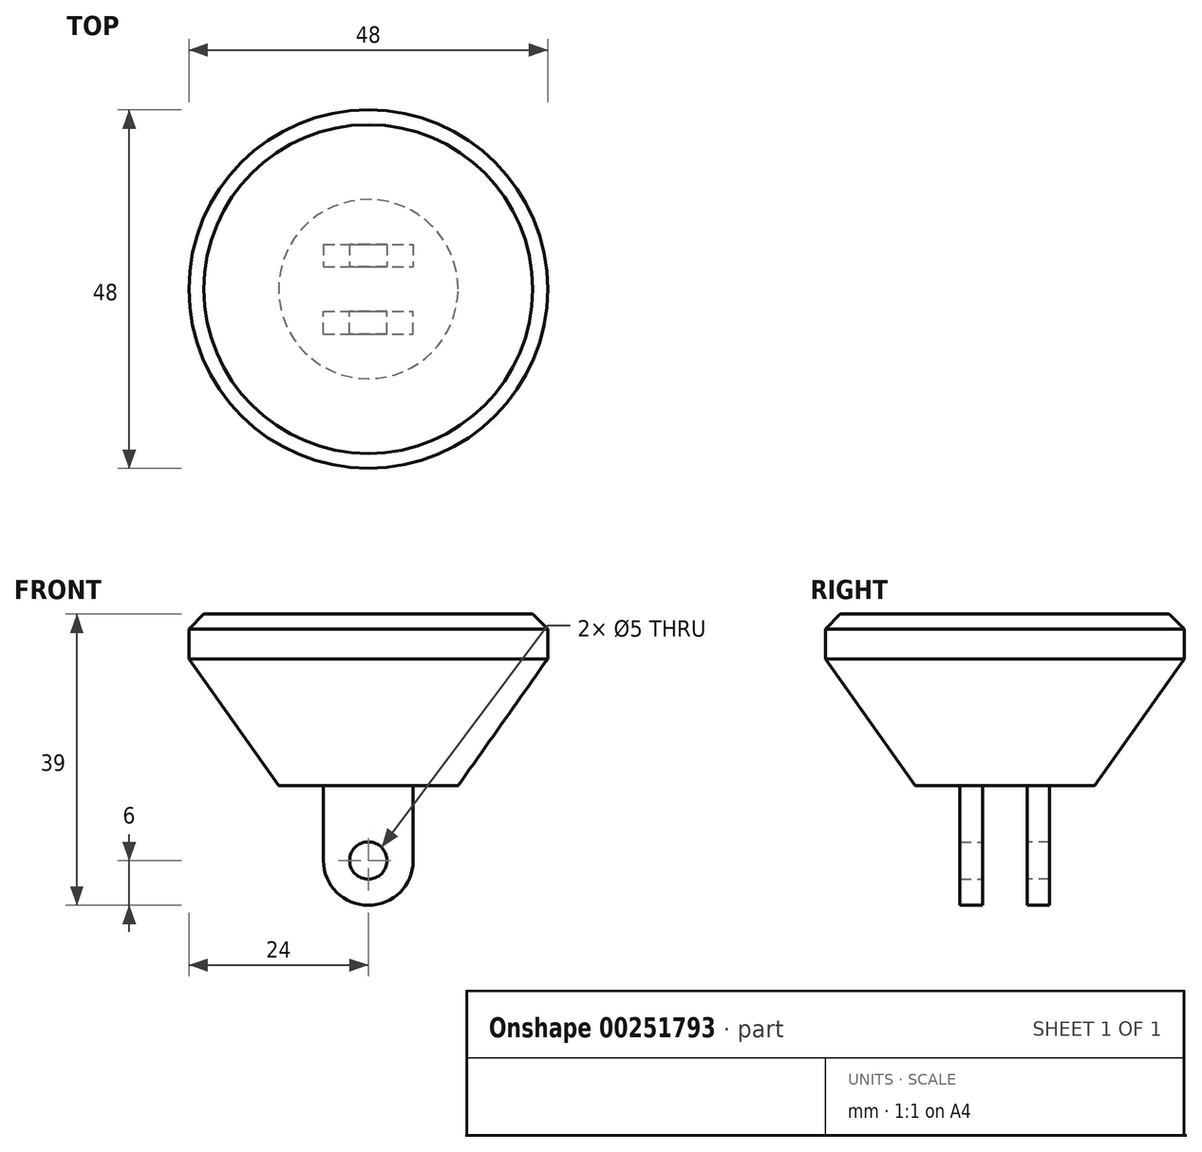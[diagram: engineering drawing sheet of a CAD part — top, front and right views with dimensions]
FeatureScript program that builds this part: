
annotation { "Feature Type Name" : "Feature", "Feature Type Description" : "" }
export const myFeature = defineFeature(function(context is Context, id is Id, definition is map)
    precondition{}
    {
        {
            var Q0;
            Q0=qCreatedBy(makeId("Top.planeOp"),FACE);
            cPlane(context, id + "F0", {"entities" : qUnion([Q0]), "cplaneType" : CPlaneType.OFFSET, "offset" : 2 * mm, "width" : 150 * mm, "height" : 150 * mm});
        }
        {
            var Q0;
            Q0=qCreatedBy(makeId("Top.planeOp"),FACE);
            cPlane(context, id + "F1", {"entities" : qUnion([Q0]), "cplaneType" : CPlaneType.OFFSET, "offset" : 4 * mm, "oppositeDirection" : true, "width" : 150 * mm, "height" : 150 * mm});
        }
        {
            var Q0;
            Q0=qCreatedBy(makeId("Top.planeOp"),FACE);
            cPlane(context, id + "F2", {"entities" : qUnion([Q0]), "cplaneType" : CPlaneType.OFFSET, "offset" : 21 * mm, "oppositeDirection" : true, "width" : 150 * mm, "height" : 150 * mm});
        }
        {
            var Q0;
            Q0=qCreatedBy(id+"F0.planeOp",FACE);
            var sketch = newSketch(context, id + "F3", { "sketchPlane" : qUnion([Q0])});
            skCircle(sketch, "E0", {"center": v(0, 0) * mm, "radius": 22 * mm});
            skSolve(sketch);
        }
        {
            var Q0;
            Q0=qCreatedBy(id+"F1.planeOp",FACE);
            var sketch = newSketch(context, id + "F4", { "sketchPlane" : qUnion([Q0])});
            skCircle(sketch, "E1", {"center": v(0, 0) * mm, "radius": 24 * mm});
            skSolve(sketch);
        }
        {
            var Q0;
            Q0=qCreatedBy(makeId("Top.planeOp"),FACE);
            var sketch = newSketch(context, id + "F5", { "sketchPlane" : qUnion([Q0])});
            skCircle(sketch, "E2", {"center": v(0, 0) * mm, "radius": 24 * mm});
            skSolve(sketch);
        }
        {
            var Q0;
            Q0=qCreatedBy(id+"F2.planeOp",FACE);
            var sketch = newSketch(context, id + "F6", { "sketchPlane" : qUnion([Q0])});
            skCircle(sketch, "E3", {"center": v(0, 0) * mm, "radius": 12 * mm});
            skSolve(sketch);
        }
        {
            var Q0;
            Q0 = qSketchRegion(id + "F6", true);
            var Q1;
            Q1 = qSketchRegion(id + "F4", true);
            loft(context, id + "F7", {"sheetProfilesArray" : [{ "sheetProfileEntities" : qUnion([Q0]) }, { "sheetProfileEntities" : qUnion([Q1]) }]});
        }
        {
            var Q1;
            Q1=makeQuery(id+"F7.opLoft","CAP_FACE",FACE,{"disambiguationData":[OSD([makeQuery(id+"F4.imprint","IMPRINT",FACE,{"disambiguationData":[TD([[makeQuery(id+"F4.imprint","IMPRINT",EDGE,{"derivedFrom":sQuery(id+"F4.wireOp",EDGE,"E1")}),1.0]])]})])],"isStart":true});
            var Q2;
            Q2=makeQuery(id+"F5.imprint","IMPRINT",FACE,{"disambiguationData":[TD([[makeQuery(id+"F5.imprint","IMPRINT",EDGE,{"derivedFrom":sQuery(id+"F5.wireOp",EDGE,"E2")}),1.0]])]});
            loft(context, id + "F8", {"operationType" : NewBodyOperationType.ADD, "sheetProfilesArray" : [{ "sheetProfileEntities" : qUnion([Q1]) }, { "sheetProfileEntities" : qUnion([Q2]) }]});
        }
        {
            var Q1;
            Q1=makeQuery(id+"F8.opLoft","CAP_FACE",FACE,{"disambiguationData":[OSD([makeQuery(id+"F5.imprint","IMPRINT",FACE,{"disambiguationData":[TD([[makeQuery(id+"F5.imprint","IMPRINT",EDGE,{"derivedFrom":sQuery(id+"F5.wireOp",EDGE,"E2")}),1.0]])]})])],"isStart":true});
            var Q2;
            Q2=makeQuery(id+"F3.imprint","IMPRINT",FACE,{"disambiguationData":[TD([[makeQuery(id+"F3.imprint","IMPRINT",EDGE,{"derivedFrom":sQuery(id+"F3.wireOp",EDGE,"E0")}),1.0]])]});
            loft(context, id + "F9", {"operationType" : NewBodyOperationType.ADD, "sheetProfilesArray" : [{ "sheetProfileEntities" : qUnion([Q1]) }, { "sheetProfileEntities" : qUnion([Q2]) }]});
        }
        {
            var Q0;
            Q0=makeQuery(id+"F7.opLoft","CAP_FACE",FACE,{"disambiguationData":[OSD([makeQuery(id+"F6.imprint","IMPRINT",FACE,{"disambiguationData":[TD([[makeQuery(id+"F6.imprint","IMPRINT",EDGE,{"derivedFrom":sQuery(id+"F6.wireOp",EDGE,"E3")}),1.0]])]})])],"isStart":true});
            var sketch = newSketch(context, id + "F10", { "sketchPlane" : qUnion([Q0])});
            skLineSegment(sketch, "E4.bottom", {"start": v(-6, -6) * mm, "end": v(6, -6) * mm});
            skLineSegment(sketch, "E4.top", {"start": v(-6, -3) * mm, "end": v(6, -3) * mm});
            skLineSegment(sketch, "E4.left", {"start": v(-6, -6) * mm, "end": v(-6, -3) * mm});
            skLineSegment(sketch, "E4.right", {"start": v(6, -6) * mm, "end": v(6, -3) * mm});
            skPoint(sketch, "E4.middle", {"position": v(0, -4.5) * mm});
            skSolve(sketch);
        }
        {
            var Q0;
            Q0 = qSketchRegion(id + "F10", true);
            extrude(context, id + "F11", {"entities" : qUnion([Q0]), "operationType" : NewBodyOperationType.ADD, "depth" : 10 * mm});
        }
        {
            var Q0;
            Q0=makeQuery(id+"F11.opExtrude","SWEPT_FACE",FACE,{"disambiguationData":[OSD([sQuery(id+"F10.wireOp",EDGE,"E4.top")])]});
            var sketch = newSketch(context, id + "F12", { "sketchPlane" : qUnion([Q0])});
            skCircle(sketch, "E5", {"center": v(0, -31) * mm, "radius": 6 * mm});
            skSolve(sketch);
        }
        {
            var Q0;
            Q0 = qSketchRegion(id + "F12", true);
            extrude(context, id + "F13", {"entities" : qUnion([Q0]), "operationType" : NewBodyOperationType.ADD, "oppositeDirection" : true, "depth" : 3 * mm});
        }
        {
            var Q0;
            Q0=makeQuery(id+"F13.boolean.opBoolean","MERGE",FACE,{"derivedFrom":[makeQuery(id+"F11.opExtrude","SWEPT_FACE",FACE,{"disambiguationData":[OSD([sQuery(id+"F10.wireOp",EDGE,"E4.top")])]}),makeQuery(id+"F13.opExtrude","CAP_FACE",FACE,{"disambiguationData":[OSD([sQuery(id+"F12.wireOp",EDGE,"E5")])],"isStart":true})]});
            var sketch = newSketch(context, id + "F14", { "sketchPlane" : qUnion([Q0])});
            skCircle(sketch, "E6", {"center": v(0, -31) * mm, "radius": 2.5 * mm});
            skSolve(sketch);
        }
        {
            var Q0;
            Q0 = qSketchRegion(id + "F14", true);
            extrude(context, id + "F15", {"entities" : qUnion([Q0]), "operationType" : NewBodyOperationType.REMOVE, "endBound" : BoundingType.THROUGH_ALL, "oppositeDirection" : true, "depth" : 25 * mm});
        }
        {
            var Q0;
            Q0=makeQuery(id+"F7.opLoft","SWEPT_BODY",BODY,{"disambiguationData":[OSD([makeQuery(id+"F4.imprint","IMPRINT",FACE,{"disambiguationData":[TD([[makeQuery(id+"F4.imprint","IMPRINT",EDGE,{"derivedFrom":sQuery(id+"F4.wireOp",EDGE,"E1")}),1.0]])]}),makeQuery(id+"F6.imprint","IMPRINT",FACE,{"disambiguationData":[TD([[makeQuery(id+"F6.imprint","IMPRINT",EDGE,{"derivedFrom":sQuery(id+"F6.wireOp",EDGE,"E3")}),1.0]])]})])]});
            var Q1;
            Q1=qCreatedBy(makeId("Front.planeOp"),FACE);
            mirror(context, id + "F16", {"operationType" : NewBodyOperationType.ADD, "entities" : qUnion([Q0]), "mirrorPlane" : qUnion([Q1])});
        }
    });
